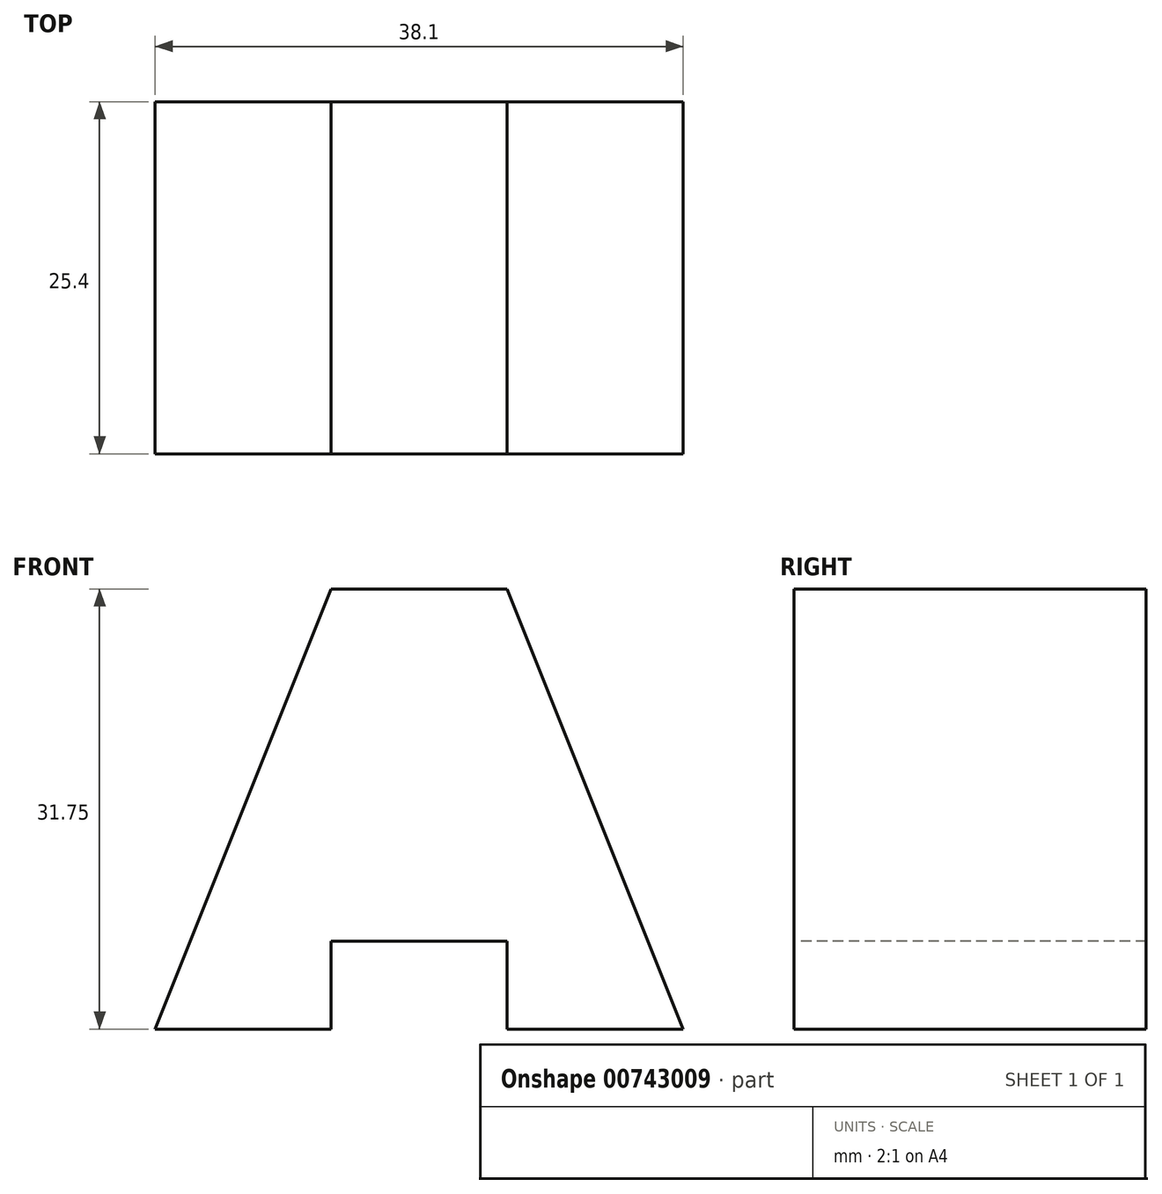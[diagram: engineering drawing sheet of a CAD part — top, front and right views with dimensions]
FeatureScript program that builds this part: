
annotation { "Feature Type Name" : "Feature", "Feature Type Description" : "" }
export const myFeature = defineFeature(function(context is Context, id is Id, definition is map)
    precondition{}
    {
        {
            var Q0;
            Q0=qCreatedBy(makeId("Front.planeOp"),FACE);
            var sketch = newSketch(context, id + "F0", { "sketchPlane" : qUnion([Q0])});
            skLineSegment(sketch, "E0", {"start": v(0, 0) * mm, "end": v(38.1, 0) * mm});
            skLineSegment(sketch, "E1", {"start": v(38.1, 0) * mm, "end": v(38.1, 31.75) * mm});
            skLineSegment(sketch, "E2", {"start": v(38.1, 31.75) * mm, "end": v(0, 31.75) * mm});
            skLineSegment(sketch, "E3", {"start": v(0, 31.75) * mm, "end": v(0, 0) * mm});
            skSolve(sketch);
        }
        {
            var Q0;
            Q0=makeQuery(id+"F0.imprint","IMPRINT",FACE,{"disambiguationData":[TD([[makeQuery(id+"F0.imprint","IMPRINT",EDGE,{"derivedFrom":sQuery(id+"F0.wireOp",EDGE,"E0")}),1.0]])]});
            extrude(context, id + "F1", {"entities" : qUnion([Q0]), "depth" : 25.4 * mm, "offsetDistance" : 25.4 * mm});
        }
        {
            var Q0;
            Q0=makeQuery(id+"F1.opExtrude","CAP_FACE",FACE,{"disambiguationData":[OSD([sQuery(id+"F0.wireOp",EDGE,"E0"),sQuery(id+"F0.wireOp",EDGE,"E1"),sQuery(id+"F0.wireOp",EDGE,"E2"),sQuery(id+"F0.wireOp",EDGE,"E3")])],"isStart":false});
            var sketch = newSketch(context, id + "F2", { "sketchPlane" : qUnion([Q0])});
            skLineSegment(sketch, "E4", {"start": v(12.7, 0) * mm, "end": v(12.7, 6.35) * mm});
            skLineSegment(sketch, "E5", {"start": v(12.7, 6.35) * mm, "end": v(25.4, 6.35) * mm});
            skLineSegment(sketch, "E6", {"start": v(25.4, 6.35) * mm, "end": v(25.4, 0) * mm});
            skLineSegment(sketch, "E7", {"start": v(25.4, 0) * mm, "end": v(12.7, 0) * mm});
            skSolve(sketch);
        }
        {
            var Q0;
            Q0=makeQuery(id+"F2.imprint","IMPRINT",FACE,{"disambiguationData":[TD([[makeQuery(id+"F2.imprint","IMPRINT",EDGE,{"derivedFrom":sQuery(id+"F2.wireOp",EDGE,"E4")}),-1.0]])]});
            extrude(context, id + "F3", {"entities" : qUnion([Q0]), "operationType" : NewBodyOperationType.REMOVE, "oppositeDirection" : true, "depth" : 25.4 * mm, "offsetDistance" : 25.4 * mm});
        }
        {
            var Q0;
            Q0=makeQuery(id+"F1.opExtrude","CAP_FACE",FACE,{"disambiguationData":[OSD([sQuery(id+"F0.wireOp",EDGE,"E0"),sQuery(id+"F0.wireOp",EDGE,"E1"),sQuery(id+"F0.wireOp",EDGE,"E2"),sQuery(id+"F0.wireOp",EDGE,"E3")])],"isStart":false});
            var sketch = newSketch(context, id + "F4", { "sketchPlane" : qUnion([Q0])});
            skLineSegment(sketch, "E8", {"start": v(0, 0) * mm, "end": v(12.7, 31.75) * mm});
            skLineSegment(sketch, "E9", {"start": v(12.7, 31.75) * mm, "end": v(0, 31.75) * mm});
            skLineSegment(sketch, "E10", {"start": v(0, 31.75) * mm, "end": v(0, 0) * mm});
            skLineSegment(sketch, "E11", {"start": v(38.1, 0) * mm, "end": v(25.4, 31.75) * mm});
            skLineSegment(sketch, "E12", {"start": v(25.4, 31.75) * mm, "end": v(38.1, 31.75) * mm});
            skLineSegment(sketch, "E13", {"start": v(38.1, 31.75) * mm, "end": v(38.1, 0) * mm});
            skSolve(sketch);
        }
        {
            var Q0;
            Q0=makeQuery(id+"F4.imprint","IMPRINT",FACE,{"disambiguationData":[TD([[makeQuery(id+"F4.imprint","IMPRINT",EDGE,{"derivedFrom":sQuery(id+"F4.wireOp",EDGE,"E8")}),1.0]])]});
            var Q1;
            Q1=makeQuery(id+"F4.imprint","IMPRINT",FACE,{"disambiguationData":[TD([[makeQuery(id+"F4.imprint","IMPRINT",EDGE,{"derivedFrom":sQuery(id+"F4.wireOp",EDGE,"E11")}),-1.0]])]});
            extrude(context, id + "F5", {"entities" : qUnion([Q0, Q1]), "operationType" : NewBodyOperationType.REMOVE, "oppositeDirection" : true, "depth" : 25.4 * mm, "offsetDistance" : 25.4 * mm});
        }
    });
